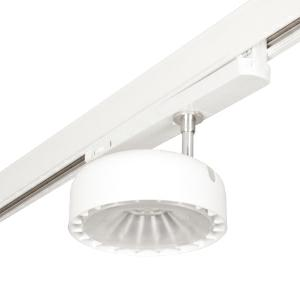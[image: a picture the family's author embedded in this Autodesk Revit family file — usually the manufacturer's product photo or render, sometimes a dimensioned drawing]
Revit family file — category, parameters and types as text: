
# Revit family: 3f_filippi_-_3f_emilio_track_ellittico_-_meat_bread_crisp_3f_filippi_-_47612_-_3f_emilio_tk_led_2000-meat_ell_1802
name_source: partatom
category: Lighting Fixtures
units: mm (PartAtom-declared; Revit-internal decimal feet)

## family parameters
Cut with Voids When Loaded = No
Host = Face
Light Source = No
Part Type = Normal
Room Calculation Point = No
Round Connector Dimension = Use Diameter
Shared = No

## types (1)
- 3F Filippi - 3F Emilio Track Ellittico - Meat/Bread/Crisp (1 x LED, 2215 lm, 32 W, 3000 K)
    Apparent Load = 32 VA
    Approval mark = CE
    CIE Flux Codes = 84 95 99 100 100
    Color Rendering = 87
    Color Temperature = 3000 K
    Control Gear = Electronic ballast
    Default Elevation = 1800 mm
    Description = Adjustable spot light with minimal dimensions for accent lighting, to be integrated into the busbar.

ILLUMINOTECHNICAL
Luminous efficiency 100% (DLOR 100%, ULOR 0%).
Initial luminous flux of the luminaire 2215 lm.
Symmetrical and elliptical distribution.
Tabular UGR (CIE 117 - 4H-8H; S=0.25H; 70/50/20): RUG 20.4 - 24.8.
Beam angle: 46° - 89°.
Luminous efficacy 69 lm/W.
Lifetime (L90/B20): 30000 h. (tq+25°C)
Lifetime (L80/B20): 50000 h. (tq+25°C)
Sudden decreased luminous flux after 50000 hours: 0% (C0).
Photobiological safety in compliance with IEC/TR 62778: RG1 low risk, (IEC 62471).
In compliance with IEC/EN 62722-2-1 - IEC/EN 62717 standards.

SOURCE
Compact LED module 2000/MEAT specific for meat.
Energy efficiency class (UE 2019/2020 - UE 2019/2015): E.
CIE 13.3 Colour rendering index: CRI 87 (R9 >50%).
IES TM-30 Fidelity Index: Rf = 80 Rg = 113.
CCT nominal colour temperature 3000 K.
Colour initial tolerance (MacAdam): SDCM 3.
Zhaga Book 3 compliant.

MECHANICAL
Wired unit in white polycarbonate with busbar adaptor.
Single-piece in die-cast aluminium with passive dissipation, white colour, with perimeter cooling slots on upper edge, giving a crown of light effect to the fitting.
Invisible lock for positioning the luminous flux.
Lens made from transparent methacrylate (PMMA) with glossy surface and differentiated photo-etched.
Positioning arm in galvanised brass with sphere to allow for vertical positioning at angles from 0° to 90° and horizontal positioning from 0° to 290°.
Dimensions: diameter 130 mm, length 230 mm, height 105 mm. Weight 0.825 kg.
IP20 protection degree.
Glow-wire test resistance 650°C.

ELECTRICAL
Wiring unit separate from the body, invisible and integrated into the busbar.
Halogen Free electronic wiring 230V-50/60Hz, power factor 0.95, THD <25%, constant output current, SELV, class II, 1 driver.
Power of the luminaire 32 W.
ENEC - CE.
SAFE FLICKER: PstLM=<1 and SVM=<0.4 (IEC TR 61547-1 and IEC TR 63158), to ensure a more comfortable and safe light.
Ambient temperature from 0°C to +25°C.
Temperature class T6 max 85°C.
Relative humidity UR: <85%.

INSTALLATION
Track.

APPLICATIONS
Transit areas, spotlighting in commercial environments, exhibition areas, restaurants, shops and shop windows.

WARNING
Luminaire designed for disposal/recycling at end-of-life.
Replaceable (LED only) light source by a professional. Replaceable control gear by a professional.
    Height = 105 mm
    Lamp = 1 x LED
    Lamp Light Flux = 2215 lm
    Lamp Power = 32 W
    Lamp count = 1
    Length = 230 mm
    Lifetime = 50000 h
    Luminous efficacy = 69 lm/W
    Manufacturer = 3F Filippi
    ModVariant = No
    Model = 3F Filippi - 47612 - 3F Emilio TK LED 2000-MEAT ELL
    Mounting Place = Ceiling
    Mounting Type = Rail mounted
    Number of Poles = 1
    OnlyDefault = Yes
    Power Factor = 1
    Product Name = 3F Filippi - 3F Emilio Track Ellittico - Meat/Bread/Crisp
    Product group = track mounted spotlight
    ProductGroupID = 12
    Protection Class = Protection class II
    Protection Degree = IP 20
    RLX_Detail_Level = 1
    RLX_Emergency_Light_Flux = 0 lm
    RLX_Emergency_Type = 0
    RLX_Emergency_Type_DB = No
    RlxData = <blob elided: 153909 chars, md5=f8cd196f>
    Socket = socket
    Standby Power = 0 W
    System Light Flux = 2215 lm
    System Power = 32 W
    Type Comments = Product without accessories
    Type Image = 3ffilippi_47612.jpg
    URL = http://relux.com
    VarID = ---
    Voltage = 0 V
    Weight = 0.00 kg
    Width = 130 mm

## geometry (parser evidence)
native form markers: Blend x4, Sweep x14
no freeform markers — native parametric forms only
